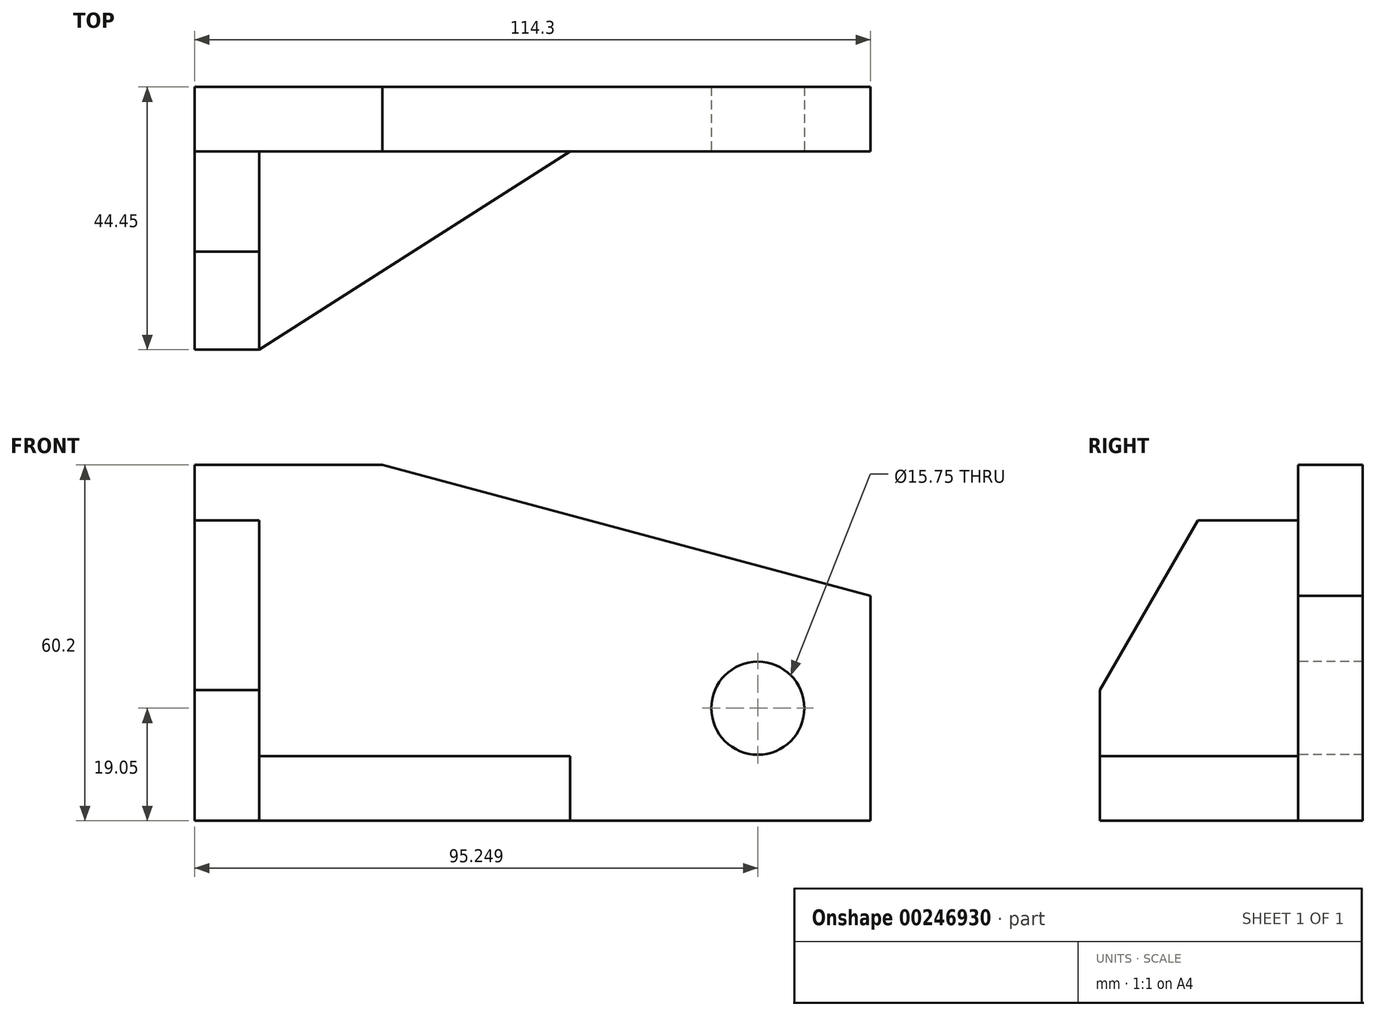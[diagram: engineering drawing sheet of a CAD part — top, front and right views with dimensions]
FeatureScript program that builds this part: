
annotation { "Feature Type Name" : "Feature", "Feature Type Description" : "" }
export const myFeature = defineFeature(function(context is Context, id is Id, definition is map)
    precondition{}
    {
        {
            var Q0;
            Q0=qCreatedBy(makeId("Front.planeOp"),FACE);
            var sketch = newSketch(context, id + "F0", { "sketchPlane" : qUnion([Q0])});
            skLineSegment(sketch, "E0.bottom", {"start": v(-5.46, 25.4) * mm, "end": v(5.46, 25.4) * mm});
            skLineSegment(sketch, "E0.top", {"start": v(-5.46, -25.4) * mm, "end": v(5.46, -25.4) * mm});
            skLineSegment(sketch, "E0.left", {"start": v(-5.46, 25.4) * mm, "end": v(-5.46, -25.4) * mm});
            skLineSegment(sketch, "E0.right", {"start": v(5.46, 25.4) * mm, "end": v(5.46, -25.4) * mm});
            skPoint(sketch, "E0.middle", {"position": v(0, 0) * mm});
            skSolve(sketch);
        }
        {
            var Q0;
            Q0=makeQuery(id+"F0.imprint","IMPRINT",FACE,{"disambiguationData":[TD([[makeQuery(id+"F0.imprint","IMPRINT",EDGE,{"derivedFrom":sQuery(id+"F0.wireOp",EDGE,"E0.bottom")}),-1.0]])]});
            extrude(context, id + "F1", {"entities" : qUnion([Q0]), "depth" : 33.53 * mm});
        }
        {
            var Q0;
            Q0=makeQuery(id+"F1.opExtrude","SWEPT_FACE",FACE,{"disambiguationData":[OSD([sQuery(id+"F0.wireOp",EDGE,"E0.right")])]});
            var sketch = newSketch(context, id + "F2", { "sketchPlane" : qUnion([Q0])});
            skLineSegment(sketch, "E1.bottom", {"start": v(-33.53, -25.4) * mm, "end": v(0, -25.4) * mm});
            skLineSegment(sketch, "E1.top", {"start": v(-33.53, -14.48) * mm, "end": v(0, -14.48) * mm});
            skLineSegment(sketch, "E1.left", {"start": v(-33.53, -25.4) * mm, "end": v(-33.53, -14.48) * mm});
            skLineSegment(sketch, "E1.right", {"start": v(0, -25.4) * mm, "end": v(0, -14.48) * mm});
            skSolve(sketch);
        }
        {
            var Q0;
            Q0=makeQuery(id+"F2.imprint","IMPRINT",FACE,{"disambiguationData":[TD([[makeQuery(id+"F2.imprint","IMPRINT",EDGE,{"derivedFrom":sQuery(id+"F2.wireOp",EDGE,"E1.bottom")}),1.0]])]});
            extrude(context, id + "F3", {"entities" : qUnion([Q0]), "operationType" : NewBodyOperationType.ADD, "depth" : 52.58 * mm});
        }
        {
            var Q0;
            Q0=makeQuery(id+"F3.boolean.opBoolean","MERGE",FACE,{"derivedFrom":[makeQuery(id+"F1.opExtrude","CAP_FACE",FACE,{"disambiguationData":[OSD([sQuery(id+"F0.wireOp",EDGE,"E0.bottom"),sQuery(id+"F0.wireOp",EDGE,"E0.top"),sQuery(id+"F0.wireOp",EDGE,"E0.left"),sQuery(id+"F0.wireOp",EDGE,"E0.right")])],"isStart":true}),makeQuery(id+"F3.opExtrude","SWEPT_FACE",FACE,{"disambiguationData":[OSD([sQuery(id+"F2.wireOp",EDGE,"E1.right")])]})]});
            var sketch = newSketch(context, id + "F4", { "sketchPlane" : qUnion([Q0])});
            skLineSegment(sketch, "E2.bottom", {"start": v(5.46, -25.4) * mm, "end": v(-108.84, -25.4) * mm});
            skLineSegment(sketch, "E2.top", {"start": v(5.46, 34.8) * mm, "end": v(-108.84, 34.8) * mm});
            skLineSegment(sketch, "E2.left", {"start": v(5.46, -25.4) * mm, "end": v(5.46, 34.8) * mm});
            skLineSegment(sketch, "E2.right", {"start": v(-108.84, -25.4) * mm, "end": v(-108.84, 34.8) * mm});
            skSolve(sketch);
        }
        {
            var Q0;
            {var subQ2=sQuery(id+"F4.wireOp",EDGE,"E2.top");Q0=makeQuery(id+"F4.imprint","IMPRINT",FACE,{"disambiguationData":[TD([[makeQuery(id+"F4.imprint","IMPRINT",EDGE,{"derivedFrom":subQ2}),1.0]])]});}
            var Q1;
            {var subQ3=makeQuery(id+"F1.opExtrude","CAP_EDGE",EDGE,{"disambiguationData":[OSD([sQuery(id+"F0.wireOp",EDGE,"E0.bottom")])],"isStart":true});Q1=makeQuery(id+"F4.imprint","IMPRINT",FACE,{"disambiguationData":[TD([[makeQuery(id+"F4.imprint","IMPRINT",EDGE,{"derivedFrom":subQ3}),1.0]])]});}
            extrude(context, id + "F5", {"entities" : qUnion([Q0, Q1]), "operationType" : NewBodyOperationType.ADD, "depth" : 10.92 * mm});
        }
        {
            var Q0;
            Q0=makeQuery(id+"F3.opExtrude","CAP_EDGE",EDGE,{"disambiguationData":[OSD([sQuery(id+"F2.wireOp",EDGE,"E1.left")])],"isStart":false});
            chamfer(context, id + "F6", {"entities" : qUnion([Q0]), "chamferType" : ChamferType.TWO_OFFSETS, "width1" : 33.53 * mm, "oppositeDirection" : false, "width2" : 52.58 * mm, "tangentPropagation" : true});
        }
        {
            var Q0;
            Q0=makeQuery(id+"F1.opExtrude","CAP_EDGE",EDGE,{"disambiguationData":[OSD([sQuery(id+"F0.wireOp",EDGE,"E0.bottom")])],"isStart":false});
            chamfer(context, id + "F7", {"entities" : qUnion([Q0]), "chamferType" : ChamferType.OFFSET_ANGLE, "width" : 28.7 * mm, "oppositeDirection" : true, "angle" : 30 * degree, "tangentPropagation" : true});
        }
        {
            var Q0;
            Q0=makeQuery(id+"F5.opExtrude","SWEPT_EDGE",EDGE,{"disambiguationData":[OSD([sQuery(id+"F4.wireOp",EDGE,"E2.top"),sQuery(id+"F4.wireOp",EDGE,"E2.right")])]});
            chamfer(context, id + "F8", {"entities" : qUnion([Q0]), "chamferType" : ChamferType.OFFSET_ANGLE, "width" : 82.55 * mm, "oppositeDirection" : true, "angle" : 15 * degree, "tangentPropagation" : true});
        }
        {
            var Q0;
            Q0=makeQuery(id+"F5.opExtrude","CAP_FACE",FACE,{"disambiguationData":[OSD([sQuery(id+"F4.wireOp",EDGE,"E2.bottom"),sQuery(id+"F4.wireOp",EDGE,"E2.top"),sQuery(id+"F4.wireOp",EDGE,"E2.left"),sQuery(id+"F4.wireOp",EDGE,"E2.right")])],"isStart":true});
            var sketch = newSketch(context, id + "F9", { "sketchPlane" : qUnion([Q0])});
            skCircle(sketch, "E3", {"center": v(89.79, -6.35) * mm, "radius": 7.87 * mm});
            skLineSegment(sketch, "E4", {"start": v(116.54, -25.4) * mm, "end": v(116.54, -6.35) * mm, "construction": true});
            skLineSegment(sketch, "E5", {"start": v(108.84, -34.6) * mm, "end": v(89.79, -34.6) * mm, "construction": true});
            skSolve(sketch);
        }
        {
            var Q0;
            Q0=makeQuery(id+"F9.imprint","IMPRINT",FACE,{"disambiguationData":[TD([[makeQuery(id+"F9.imprint","IMPRINT",EDGE,{"derivedFrom":sQuery(id+"F9.wireOp",EDGE,"E3")}),1.0]])]});
            extrude(context, id + "F10", {"entities" : qUnion([Q0]), "operationType" : NewBodyOperationType.REMOVE, "oppositeDirection" : true, "depth" : 10.92 * mm});
        }
    });
